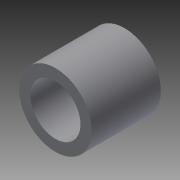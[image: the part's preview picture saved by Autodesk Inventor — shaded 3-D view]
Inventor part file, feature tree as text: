
AUTODESK INVENTOR PART (.ipt)
format: ipt  version: 2013 (Build 170138000, 138)  size: 78,336 bytes
history: native  units: mm
features: other x1, extrude x1, sketch x1
ambient origin geometry x8: Origin, YZ Plane, XZ Plane, XY Plane, X Axis, Y Axis, Z Axis, Center Point
feature tree (3):
  other  "ソリッド1"
  extrude  "押し出し1"  Depth=14.5mm
  sketch  "スケッチ1"
